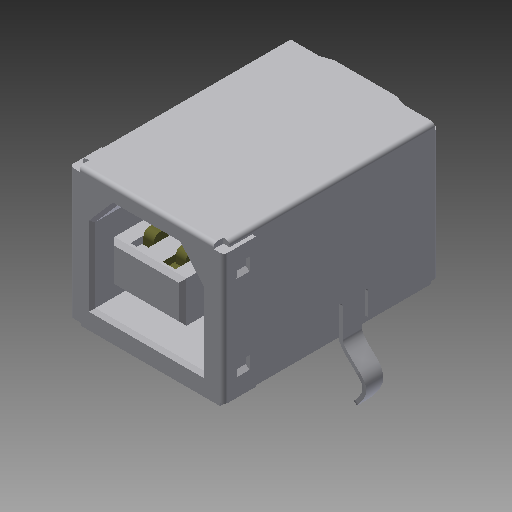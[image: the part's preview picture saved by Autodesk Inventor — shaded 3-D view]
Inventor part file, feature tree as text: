
AUTODESK INVENTOR PART (.ipt)
format: ipt  version: 2019 (Build 230136000, 136)  size: 466,944 bytes
history: native  units: mm
features: mirror x1, imported_body x1
ambient origin geometry x8: Origin, YZ Plane, XZ Plane, XY Plane, X Axis, Y Axis, Z Axis, Center Point
bodies: Body1 (feature_tree)
feature tree (2):
  mirror  "Mirror17"
  imported_body  "Base1"
